# Revit family: GR_Решетка_РАД(Р)_Вытяжка_LOD400_R21
name_source: partatom
category: Воздухораспределители
units: mm (PartAtom-declared; Revit-internal decimal feet)

## family parameters
Всегда вертикально = Да
Заголовок OmniClass = Diffusers, Registers, and Grilles
На основе рабочей плоскости = Нет
Номер OmniClass = 23.75.70.21.27.11
Общий = Нет
При загрузке вырезать с полостями = Да
Размер круглого соединителя = Использовать диаметр
Тип детали = Нормальный
Точка принадлежности помещению = Нет

## types (2) — shared parameters
ADSK_URL страницы изделия = https://grilles.ru
ADSK_Автор = THE GRILLES
ADSK_Версия Revit = 2021
ADSK_Версия семейства = v1
ADSK_Единица измерения = шт.
ADSK_Завод-изготовитель = ООО "ВЕНТРЕШЕТКИКОМ"
ADSK_Количество = 1
GR_Материал КРВ = ADSK_Оцинкованная сталь
GR_Материал решетки = Сталь, RAL 9016M, белый
URL = https://grilles.ru
Изготовитель = ООО "ВЕНТРЕШЕТКИКОМ"
О = ♠ : 0°
О15 = ♠ : 15°
О30 = ♠ : 30°
О45 = ♠ : 45°
О60 = ♠ : 60°
О75 = ♠ : 75°
О90 = ♠ : 90°
zero-valued in all types: Отметка по умолчанию

## per-type parameters (varying)
| type | ADSK_Код изделия | ADSK_Наименование | КЖС | КРВ | Описание |
| РАД | 002039 | Решетка регулируемая вытяжная РАД | 0.63 | Нет | Двухрядная регулируемая решетка РАД используются в
приточно-вытяжной вентиляции и системах кондиционирования воздуха
и предназначена для регулировки направления воздушного потока вверх/
вниз и влево/вправо. При этом можно как расширять поток так и сужать его и
направлять в определенную сторону помещения. Решетки РАД монтируются
в вентиляционные каналы и строительные проемы различных типов. |
| РАД-Р | 000165 | Решетка регулируемая вытяжная с клапаном РАД-Р | 0.58 | Да | Двухрядная регулируемая решетка РАД-Р с клапаном расхода воздуха ( КРВ) используются в приточно-вытяжной вентиляции и системах кондиционирования воздуха. Решетка предназначена для регулировки направления и объема воздушного потока вверх/вниз и влево/вправо. При этом можно как расширять поток так и сужать его и направлять в определенную сторону помещения. Монтируются решетки в вентиляционные каналы и строительные проемы различных типов. |
